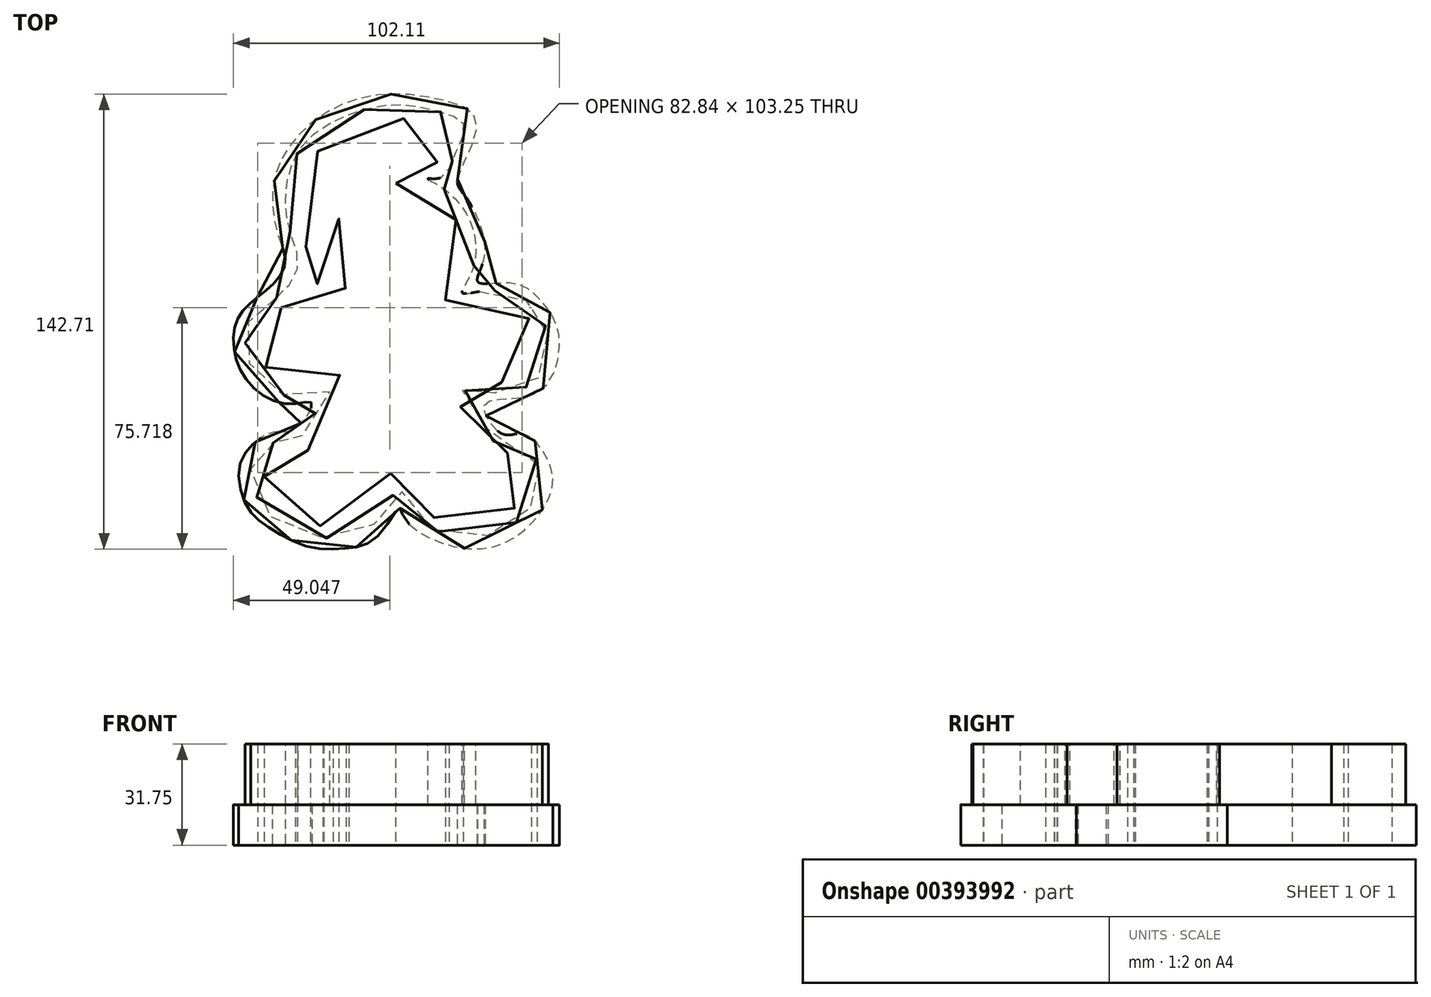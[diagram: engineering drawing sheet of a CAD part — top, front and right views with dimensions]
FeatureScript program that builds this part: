
annotation { "Feature Type Name" : "Feature", "Feature Type Description" : "" }
export const myFeature = defineFeature(function(context is Context, id is Id, definition is map)
    precondition{}
    {
        {
            var Q0;
            Q0=qCreatedBy(makeId("Top.planeOp"),FACE);
            var sketch = newSketch(context, id + "F0", { "sketchPlane" : qUnion([Q0])});
            skFitSpline(sketch, "E0", {"points": [v(2.77, 48.07) * mm, v(4.04, 51.23) * mm, v(6.56, 54.07) * mm, v(12.78, 54.07) * mm, v(14.32, 53.32) * mm, v(19.37, 63.42) * mm, v(15.75, 65.98) * mm, v(7.7, 68.06) * mm, v(-2.72, 67.77) * mm, v(-15.24, 63.3) * mm, v(-24.18, 54.95) * mm, v(-28.06, 42.43) * mm, v(-25.08, 26.94) * mm, v(-24.78, 19.78) * mm, v(-28.65, 13.82) * mm, v(-21.8, 16.5) * mm, v(-20.01, 26.64) * mm, v(-18.82, 33.5) * mm, v(-15.24, 37.07) * mm, v(-16.43, 31.1) * mm, v(-16.73, 23.36) * mm, v(-14.35, 16.8) * mm, v(-11.96, 12.73) * mm, v(-19.66, 10.97) * mm, v(-31.35, 9.54) * mm, v(-36.26, 7.28) * mm, v(-40.24, 0.64) * mm, v(-39.44, -7.19) * mm, v(-36.4, -11.3) * mm, v(-30.95, -14.22) * mm, v(-19.4, -13.3) * mm, v(-13.03, -12.37) * mm, v(-16.21, -20.6) * mm, v(-24.5, -35.1) * mm, v(-26.59, -37.48) * mm, v(-29.57, -36.58) * mm, v(-35.53, -38.07) * mm, v(-38.51, -43.74) * mm, v(-36.42, -50) * mm, v(-30.46, -55.95) * mm, v(-19.74, -59.53) * mm, v(-7.81, -56.85) * mm, v(-0.07, -45.82) * mm, v(2.92, -40.16) * mm, v(6.2, -46.12) * mm, v(12.78, -55.36) * mm, v(21.1, -59.23) * mm, v(32.12, -58.34) * mm, v(40.77, -52.97) * mm, v(44.94, -46.72) * mm, v(43.75, -40.16) * mm, v(37.79, -36.58) * mm, v(32.72, -37.18) * mm, v(28.25, -30.92) * mm, v(24.08, -23.77) * mm, v(19.6, -13.34) * mm, v(26.76, -13.34) * mm, v(36.9, -14.23) * mm, v(45.53, -8.57) * mm, v(46.43, 0.97) * mm, v(42.26, 7.82) * mm, v(30.04, 10.97) * mm, v(18.41, 10.97) * mm, v(20.5, 15.27) * mm, v(23.78, 24.81) * mm, v(21.4, 37.03) * mm, v(16.03, 43.59) * mm, v(10.07, 46.87) * mm, v(2.77, 48.07) * mm]});
            skSolve(sketch);
        }
        {
            var Q0;
            Q0=qCreatedBy(makeId("Top.planeOp"),FACE);
            var sketch = newSketch(context, id + "F1", { "sketchPlane" : qUnion([Q0])});
            skFitSpline(sketch, "E1", {"points": [v(-34.62, 12.22) * mm, v(-27.93, 22.11) * mm, v(-30.26, 32.3) * mm, v(-31.71, 45.1) * mm, v(-27.93, 57.9) * mm, v(-18.33, 66.63) * mm, v(-4.36, 71.86) * mm, v(7.28, 72.45) * mm, v(19.5, 69.54) * mm, v(24.15, 66.05) * mm, v(20.95, 56.44) * mm, v(16.88, 49.75) * mm, v(12.8, 49.46) * mm, v(17.75, 46.26) * mm, v(26.77, 34.04) * mm, v(26.19, 19.5) * mm, v(23.57, 13.68) * mm, v(30.26, 14.26) * mm, v(41.31, 12.51) * mm, v(47.42, 7.56) * mm, v(50.33, 0) * mm, v(48.88, -10.47) * mm, v(41.9, -16.58) * mm, v(31.42, -17.75) * mm, v(25.9, -17.46) * mm, v(23.57, -16.87) * mm, v(26.77, -21.82) * mm, v(33.17, -32.59) * mm, v(34.91, -34.04) * mm, v(38.99, -33.46) * mm, v(45.39, -36.66) * mm, v(48.59, -45.1) * mm, v(43.64, -55.28) * mm, v(33.46, -61.97) * mm, v(18.9, -61.97) * mm, v(8.15, -55.57) * mm, v(3.78, -48) * mm, v(-2.91, -57.6) * mm, v(-14.84, -63.13) * mm, v(-30.55, -60.51) * mm, v(-40.44, -51.2) * mm, v(-42.48, -39.86) * mm, v(-38.99, -35.2) * mm, v(-32, -32.58) * mm, v(-28.19, -33.2) * mm, v(-24.05, -26.38) * mm, v(-18.04, -17.16) * mm, v(-28.8, -18.62) * mm, v(-39.28, -14.25) * mm, v(-43.93, -5.82) * mm, v(-43.93, 2.62) * mm, v(-40.73, 8.73) * mm, v(-34.62, 12.22) * mm]});
            skSolve(sketch);
        }
        {
            var Q0;
            Q0=qSketchRegion(id+"F1",true);
            extrude(context, id + "F2", {"entities" : qUnion([Q0]), "depth" : 31.75 * mm});
        }
        {
            var Q0;
            Q0=qSketchRegion(id+"F0",true);
            extrude(context, id + "F3", {"entities" : qUnion([Q0]), "operationType" : NewBodyOperationType.REMOVE, "depth" : 38.1 * mm});
        }
        {
            var Q0;
            Q0=qCreatedBy(makeId("Top.planeOp"),FACE);
            var sketch = newSketch(context, id + "F4", { "sketchPlane" : qUnion([Q0])});
            skFitSpline(sketch, "E2", {"points": [v(22.07, 49.27) * mm, v(28.2, 67.2) * mm, v(16.87, 74.19) * mm, v(0, 75.93) * mm, v(-17.16, 71.28) * mm, v(-30.84, 59.35) * mm, v(-35.78, 46.26) * mm, v(-34.33, 32.3) * mm, v(-32.02, 22.7) * mm, v(-38.12, 14.26) * mm, v(-45.97, 6.98) * mm, v(-48, -3.5) * mm, v(-42.48, -15.42) * mm, v(-29.97, -21.24) * mm, v(-23.6, -20.96) * mm, v(-29.1, -29.09) * mm, v(-34.91, -29.97) * mm, v(-41.3, -33.17) * mm, v(-46.25, -41.02) * mm, v(-43.92, -53.24) * mm, v(-36.95, -59.93) * mm, v(-24.15, -66.04) * mm, v(-12.22, -66.33) * mm, v(-3.2, -62.84) * mm, v(3.78, -53.86) * mm, v(5.82, -57.6) * mm, v(29.1, -66.62) * mm, v(47.71, -55.56) * mm, v(51.49, -41.9) * mm, v(42.76, -30.56) * mm, v(36.08, -30.54) * mm, v(30.6, -21.25) * mm, v(46.42, -17.97) * mm, v(53.82, 0) * mm, v(48.3, 11.06) * mm, v(39.56, 16.62) * mm, v(28.42, 17.08) * mm, v(30.58, 25.63) * mm, v(24.76, 43.6) * mm, v(22.07, 49.27) * mm]});
            skSolve(sketch);
        }
        {
            var Q0;
            Q0 = qSketchRegion(id + "F4", true);
            extrude(context, id + "F5", {"entities" : qUnion([Q0]), "operationType" : NewBodyOperationType.ADD, "depth" : 12.7 * mm});
        }
        {
            var Q0;
            Q0 = qSketchRegion(id + "F0", true);
            extrude(context, id + "F6", {"entities" : qUnion([Q0]), "operationType" : NewBodyOperationType.REMOVE, "depth" : 63.5 * mm});
        }
    });
